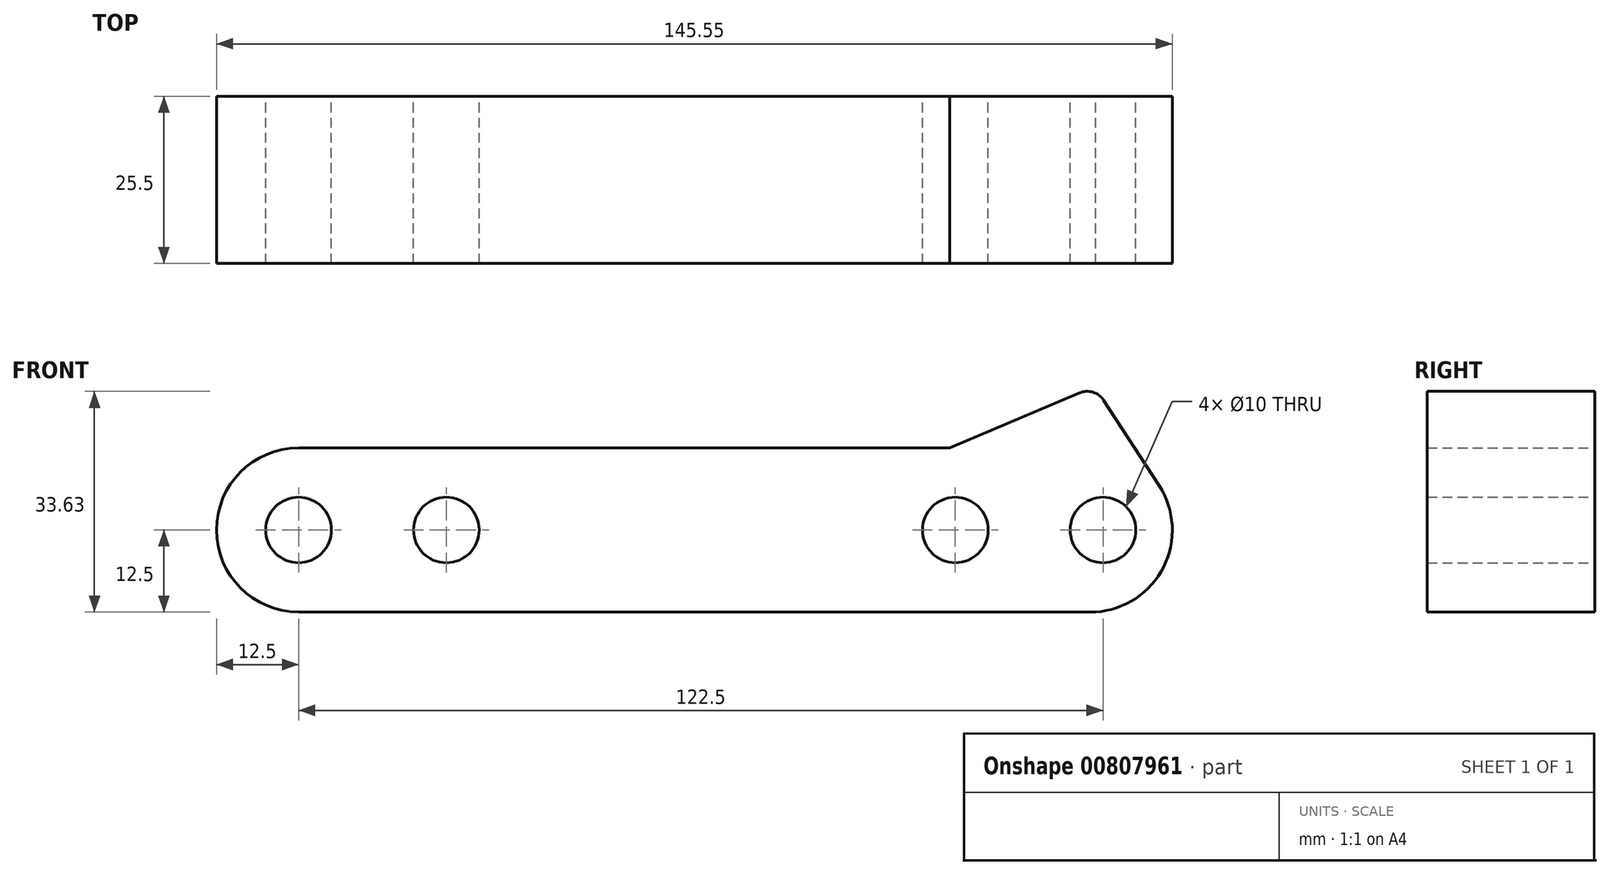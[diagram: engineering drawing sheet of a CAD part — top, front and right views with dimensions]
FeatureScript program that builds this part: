
annotation { "Feature Type Name" : "Feature", "Feature Type Description" : "" }
export const myFeature = defineFeature(function(context is Context, id is Id, definition is map)
    precondition{}
    {
        {
            var Q0;
            Q0=qCreatedBy(makeId("Front.planeOp"),FACE);
            var sketch = newSketch(context, id + "F0", { "sketchPlane" : qUnion([Q0])});
            skLineSegment(sketch, "E0.bottom", {"start": v(0, 0) * mm, "end": v(121.36, 0) * mm});
            skLineSegment(sketch, "E0.top", {"start": v(0, 25) * mm, "end": v(99.14, 25) * mm});
            skArc(sketch, "E1", {"start": v(0, 25) * mm, "mid": v(-12.5, 12.5) * mm, "end": v(0, 0) * mm});
            skCircle(sketch, "E2", {"center": v(0, 12.5) * mm, "radius": 5 * mm});
            skArc(sketch, "E3", {"start": v(121.36, 0) * mm, "mid": v(131.72, 6.87) * mm, "end": v(131.03, 19.28) * mm});
            skLineSegment(sketch, "E4", {"start": v(99.14, 25) * mm, "end": v(121.23, 34.38) * mm});
            skLineSegment(sketch, "E5", {"start": v(121.23, 34.38) * mm, "end": v(131.03, 19.28) * mm});
            skCircle(sketch, "E6", {"center": v(100, 12.5) * mm, "radius": 5 * mm});
            skCircle(sketch, "E7", {"center": v(122.5, 12.5) * mm, "radius": 5 * mm});
            skLineSegment(sketch, "E8", {"start": v(0, 12.5) * mm, "end": v(22.5, 12.5) * mm});
            skCircle(sketch, "E9", {"center": v(22.5, 12.5) * mm, "radius": 5 * mm});
            skSolve(sketch);
        }
        {
            var Q0;
            Q0=makeQuery(id+"F0.imprint","IMPRINT",FACE,{"disambiguationData":[TD([[makeQuery(id+"F0.imprint","IMPRINT",EDGE,{"derivedFrom":sQuery(id+"F0.wireOp",EDGE,"E0.bottom")}),1.0]])]});
            extrude(context, id + "F1", {"entities" : qUnion([Q0]), "depth" : 25.5 * mm, "offsetDistance" : 25 * mm});
        }
        {
            var Q0;
            Q0=qCreatedBy(makeId("Front.planeOp"),FACE);
            var sketch = newSketch(context, id + "F2", { "sketchPlane" : qUnion([Q0])});
            skCircle(sketch, "E10", {"center": v(15.16, -26.68) * mm, "radius": 30 * mm});
            skSolve(sketch);
        }
        {
            var Q0;
            Q0=makeQuery(id+"F1.opExtrude","SWEPT_EDGE",EDGE,{"disambiguationData":[OSD([sQuery(id+"F0.wireOp",EDGE,"E4"),sQuery(id+"F0.wireOp",EDGE,"E5")])]});
            fillet(context, id + "F3", {"entities" : qUnion([Q0]), "radius" : 3 * mm, "tangentPropagation" : true, "allowEdgeOverflow" : false});
        }
    });
